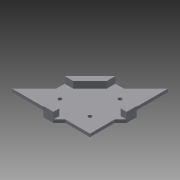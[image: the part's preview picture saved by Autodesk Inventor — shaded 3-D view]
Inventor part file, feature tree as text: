
AUTODESK INVENTOR PART (.ipt)
format: ipt  version: 2015 (Build 190159000, 159)  size: 127,488 bytes
history: native  units: in
note: dims shown in document units (in); Inventor stores cm internally (conversion verified against a paired STEP export)
features: extrude x2, sketch x1
ambient origin geometry x8: Origin, YZ Plane, XZ Plane, XY Plane, X Axis, Y Axis, Z Axis, Center Point
bodies: Body1 (feature_tree)
feature tree (3):
  sketch  "Sketch1"  dims[d36=0.9843in d38=0.9843in d42=0.1181in d43=0.1181in d44=0.1181in d45=1.0039in d47=0.0394in d51=2.5591in d52=2.5591in d54=0.1969in d55=0.1969in d56=0.1969in d57=0.0984in d58=0.0in d59=0.315in d60=0.0in]
  extrude  "Extrusion5"  Depth=0.315in
  extrude  "Extrusion6"  Depth=0.315in
